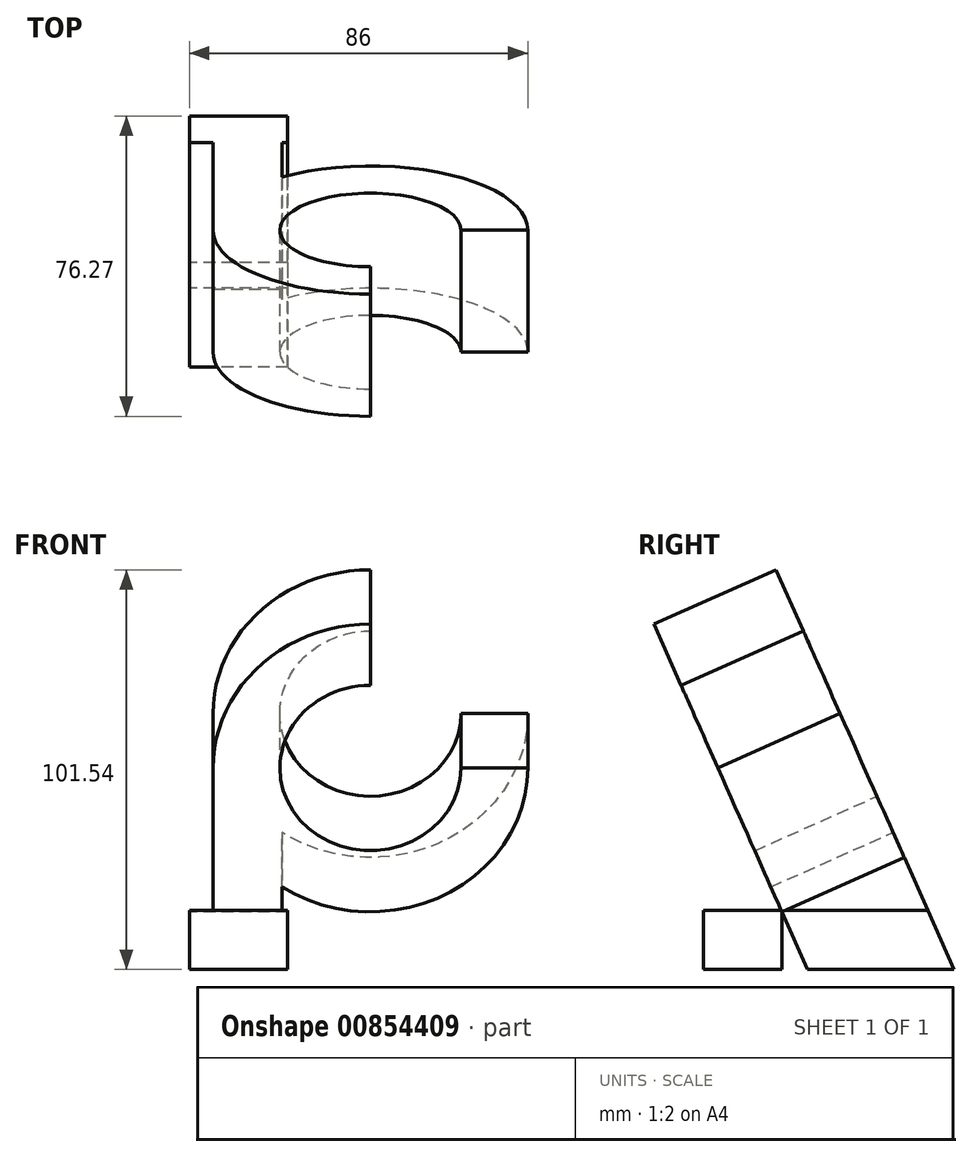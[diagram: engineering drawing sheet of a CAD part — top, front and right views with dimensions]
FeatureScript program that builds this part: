
annotation { "Feature Type Name" : "Feature", "Feature Type Description" : "" }
export const myFeature = defineFeature(function(context is Context, id is Id, definition is map)
    precondition{}
    {
        {
            var Q0;
            Q0=qCreatedBy(makeId("Top.planeOp"),FACE);
            var sketch = newSketch(context, id + "F0", { "sketchPlane" : qUnion([Q0])});
            skLineSegment(sketch, "E0", {"start": v(-57.2, 0) * mm, "end": v(54.58, 0) * mm});
            skSolve(sketch);
        }
        {
            var Q0;
            Q0 = qBodyType(qCreatedBy(id + "F0" ,EDGE), BodyType.WIRE);
            cPlane(context, id + "F1", {"entities" : qUnion([Q0]), "cplaneType" : CPlaneType.LINE_ANGLE, "offset" : 25 * mm, "angle" : 24 * degree, "width" : 150 * mm, "height" : 150 * mm});
        }
        {
            var Q0;
            Q0=qCreatedBy(id+"F1.planeOp",FACE);
            var sketch = newSketch(context, id + "F2", { "sketchPlane" : qUnion([Q0])});
            skCircle(sketch, "E1", {"center": v(0, 0) * mm, "radius": 23 * mm});
            skCircle(sketch, "E2", {"center": v(0, 0) * mm, "radius": 40 * mm});
            skSolve(sketch);
        }
        {
            var Q0;
            Q0=qCreatedBy(makeId("Right.planeOp"),FACE);
            var sketch = newSketch(context, id + "F3", { "sketchPlane" : qUnion([Q0])});
            skPoint(sketch, "E3.0", {"position": v(0, 0) * mm});
            skLineSegment(sketch, "E4.0.0", {"start": v(-9.35, 21.01) * mm, "end": v(9.35, -21.01) * mm});
            skLineSegment(sketch, "E5.0", {"start": v(-16.27, 36.54) * mm, "end": v(16.27, -36.54) * mm});
            skLineSegment(sketch, "E6", {"start": v(-39.16, -65) * mm, "end": v(50.6, -65) * mm});
            skSolve(sketch);
        }
        {
            var Q0;
            Q0=makeQuery(id+"F2.imprint","IMPRINT",FACE,{"disambiguationData":[TD([[makeQuery(id+"F2.imprint","IMPRINT",EDGE,{"derivedFrom":sQuery(id+"F2.wireOp",EDGE,"E1")}),-1.0]])]});
            extrude(context, id + "F4", {"entities" : qUnion([Q0]), "oppositeDirection" : true, "depth" : 34 * mm, "offsetDistance" : 25 * mm});
        }
        {
            var Q0;
            Q0=qCreatedBy(makeId("Right.planeOp"),FACE);
            var sketch = newSketch(context, id + "F5", { "sketchPlane" : qUnion([Q0])});
            skLineSegment(sketch, "E7.0", {"start": v(-47.33, 22.71) * mm, "end": v(-14.8, -50.37) * mm});
            skLineSegment(sketch, "E8", {"start": v(-14.8, -50.37) * mm, "end": v(1.65, -87.3) * mm});
            skLineSegment(sketch, "E9.0", {"start": v(-16.27, 36.54) * mm, "end": v(16.27, -36.54) * mm});
            skLineSegment(sketch, "E10", {"start": v(16.27, -36.54) * mm, "end": v(32.23, -72.39) * mm});
            skLineSegment(sketch, "E11.0", {"start": v(-39.16, -50) * mm, "end": v(50.6, -50) * mm});
            skLineSegment(sketch, "E12", {"start": v(-14.8, -50.37) * mm, "end": v(-14.8, -68.96) * mm});
            skLineSegment(sketch, "E13.0", {"start": v(-39.16, -65) * mm, "end": v(50.6, -65) * mm});
            skLineSegment(sketch, "E14", {"start": v(-14.8, -65) * mm, "end": v(-34.8, -65) * mm});
            skPoint(sketch, "E14.startSnap0", {"position": v(-14.8, -59.67) * mm});
            skLineSegment(sketch, "E15", {"start": v(-14.8, -65) * mm, "end": v(45.2, -65) * mm});
            skLineSegment(sketch, "E16", {"start": v(-34.8, -65) * mm, "end": v(-34.8, -50) * mm});
            skLineSegment(sketch, "E17", {"start": v(45.2, -65) * mm, "end": v(45.2, -50) * mm});
            skSolve(sketch);
        }
        {
            var Q0;
            Q0=qCreatedBy(makeId("Right.planeOp"),FACE);
            cPlane(context, id + "F6", {"entities" : qUnion([Q0]), "cplaneType" : CPlaneType.OFFSET, "offset" : 46 * mm, "oppositeDirection" : true, "width" : 150 * mm, "height" : 150 * mm});
        }
        {
            var Q0;
            Q0=qCreatedBy(id+"F6.planeOp",FACE);
            var sketch = newSketch(context, id + "F7", { "sketchPlane" : qUnion([Q0])});
            skLineSegment(sketch, "E18.0.0", {"start": v(-34.8, -50) * mm, "end": v(-34.8, -65) * mm});
            skLineSegment(sketch, "E18.0.1", {"start": v(-34.8, -65) * mm, "end": v(-14.8, -65) * mm});
            skLineSegment(sketch, "E18.0.2", {"start": v(-14.8, -65) * mm, "end": v(-14.8, -50.37) * mm});
            skLineSegment(sketch, "E18.0.3", {"start": v(-14.8, -50.37) * mm, "end": v(-14.96, -50) * mm});
            skLineSegment(sketch, "E18.0.4", {"start": v(-14.96, -50) * mm, "end": v(-34.8, -50) * mm});
            skLineSegment(sketch, "E19.0.0", {"start": v(-8.28, -65) * mm, "end": v(-14.8, -50.37) * mm});
            skLineSegment(sketch, "E19.0.1", {"start": v(-14.8, -50.37) * mm, "end": v(-14.8, -65) * mm});
            skLineSegment(sketch, "E19.0.2", {"start": v(-14.8, -65) * mm, "end": v(-8.28, -65) * mm});
            skLineSegment(sketch, "E20.0.0", {"start": v(22.26, -50) * mm, "end": v(-14.96, -50) * mm});
            skLineSegment(sketch, "E20.0.1", {"start": v(-14.96, -50) * mm, "end": v(-14.8, -50.37) * mm});
            skLineSegment(sketch, "E20.0.2", {"start": v(-14.8, -50.37) * mm, "end": v(-8.28, -65) * mm});
            skLineSegment(sketch, "E20.0.3", {"start": v(-8.28, -65) * mm, "end": v(28.94, -65) * mm});
            skLineSegment(sketch, "E20.0.4", {"start": v(28.94, -65) * mm, "end": v(22.26, -50) * mm});
            skLineSegment(sketch, "E21.0.0", {"start": v(22.26, -50) * mm, "end": v(28.94, -65) * mm});
            skLineSegment(sketch, "E21.0.1", {"start": v(28.94, -65) * mm, "end": v(45.2, -65) * mm});
            skLineSegment(sketch, "E21.0.2", {"start": v(45.2, -65) * mm, "end": v(45.2, -50) * mm});
            skLineSegment(sketch, "E21.0.3", {"start": v(45.2, -50) * mm, "end": v(22.26, -50) * mm});
            skSolve(sketch);
        }
        {
            var Q0;
            Q0=makeQuery(id+"F7.imprint","IMPRINT",FACE,{"disambiguationData":[TD([[makeQuery(id+"F7.imprint","IMPRINT",EDGE,{"derivedFrom":sQuery(id+"F7.wireOp",EDGE,"E21.0.0")}),1.0]])]});
            var Q1;
            Q1=makeQuery(id+"F7.imprint","IMPRINT",FACE,{"disambiguationData":[TD([[makeQuery(id+"F7.imprint","IMPRINT",EDGE,{"derivedFrom":sQuery(id+"F7.wireOp",EDGE,"E20.0.0")}),1.0]])]});
            var Q2;
            Q2=makeQuery(id+"F7.imprint","IMPRINT",FACE,{"disambiguationData":[TD([[makeQuery(id+"F7.imprint","IMPRINT",EDGE,{"derivedFrom":sQuery(id+"F7.wireOp",EDGE,"E19.0.1")}),1.0]])]});
            var Q3;
            Q3=makeQuery(id+"F7.imprint","IMPRINT",FACE,{"disambiguationData":[TD([[makeQuery(id+"F7.imprint","IMPRINT",EDGE,{"derivedFrom":sQuery(id+"F7.wireOp",EDGE,"E18.0.0")}),1.0]])]});
            extrude(context, id + "F8", {"entities" : qUnion([Q0, Q1, Q2, Q3]), "depth" : 25 * mm, "offsetDistance" : 25 * mm});
        }
        {
            var Q0;
            Q0=qCreatedBy(id+"F1.planeOp",FACE);
            var sketch = newSketch(context, id + "F9", { "sketchPlane" : qUnion([Q0])});
            skCircle(sketch, "E22.0.0", {"center": v(0, 0) * mm, "radius": 40 * mm});
            skLineSegment(sketch, "E23.0", {"start": v(57.2, 0) * mm, "end": v(-54.58, 0) * mm});
            skLineSegment(sketch, "E24", {"start": v(40, 0) * mm, "end": v(40, -135.38) * mm});
            skLineSegment(sketch, "E25", {"start": v(22.5, 0) * mm, "end": v(22.5, -138.62) * mm});
            skLineSegment(sketch, "E26", {"start": v(22.5, -125.31) * mm, "end": v(40, -125.31) * mm});
            skSolve(sketch);
        }
        {
            var Q0;
            {var subQ5=sQuery(id+"F9.wireOp",EDGE,"E26");Q0=makeQuery(id+"F9.imprint","IMPRINT",FACE,{"disambiguationData":[TD([[makeQuery(id+"F9.imprint","IMPRINT",EDGE,{"derivedFrom":subQ5}),1.0]])]});}
            var Q1;
            Q1=makeQuery(id+"F4.opExtrude","CAP_FACE",FACE,{"disambiguationData":[OSD([sQuery(id+"F2.wireOp",EDGE,"E1"),sQuery(id+"F2.wireOp",EDGE,"E2")])],"isStart":false});
            extrude(context, id + "F10", {"entities" : qUnion([Q0]), "operationType" : NewBodyOperationType.ADD, "endBound" : BoundingType.UP_TO_SURFACE, "oppositeDirection" : true, "depth" : 25 * mm, "endBoundEntityFace" : qUnion([Q1]), "offsetDistance" : 25 * mm});
        }
        {
            var Q0;
            {var subQ0=sQuery(id+"F9.wireOp",EDGE,"E26");var subQ1=sQuery(id+"F9.wireOp",EDGE,"E25");Q0=makeQuery(id+"F10.boolean.opBoolean","SPLIT",FACE,{"disambiguationData":[TD([makeQuery(id+"F10.opExtrude","SWEPT_FACE",FACE,{"disambiguationData":[OSD([subQ0])]})])],"derivedFrom":makeQuery(id+"F10.opExtrude","SWEPT_FACE",FACE,{"disambiguationData":[OSD([subQ1])]})});}
            extrude(context, id + "F11", {"entities" : qUnion([Q0]), "operationType" : NewBodyOperationType.REMOVE, "oppositeDirection" : true, "depth" : 133 * mm, "offsetDistance" : 25 * mm});
        }
        {
            var Q0;
            Q0=makeQuery(id+"F10.boolean.opBoolean","MERGE",FACE,{"derivedFrom":[makeQuery(id+"F4.opExtrude","CAP_FACE",FACE,{"disambiguationData":[OSD([sQuery(id+"F2.wireOp",EDGE,"E1"),sQuery(id+"F2.wireOp",EDGE,"E2")])],"isStart":true}),makeQuery(id+"F10.opExtrude","CAP_FACE",FACE,{"disambiguationData":[OSD([sQuery(id+"F9.wireOp",EDGE,"E22.0.0"),sQuery(id+"F9.wireOp",EDGE,"E24"),sQuery(id+"F9.wireOp",EDGE,"E25"),sQuery(id+"F9.wireOp",EDGE,"E26")])],"isStart":true})]});
            var sketch = newSketch(context, id + "F12", { "sketchPlane" : qUnion([Q0])});
            skArc(sketch, "E27.0.0", {"start": v(40, 0) * mm, "mid": v(-35.36, 18.7) * mm, "end": v(22.5, -33.07) * mm});
            skLineSegment(sketch, "E27.0.1", {"start": v(22.5, -33.07) * mm, "end": v(22.5, -54.73) * mm});
            skLineSegment(sketch, "E27.0.2", {"start": v(22.5, -54.73) * mm, "end": v(40, -54.73) * mm});
            skLineSegment(sketch, "E27.0.3", {"start": v(40, -54.73) * mm, "end": v(40, 0) * mm});
            skCircle(sketch, "E28.0", {"center": v(0, 0) * mm, "radius": 23 * mm});
            skLineSegment(sketch, "E29", {"start": v(0, 23) * mm, "end": v(0, 40) * mm});
            skLineSegment(sketch, "E30", {"start": v(-23, 0) * mm, "end": v(-40, 0) * mm});
            skSolve(sketch);
        }
        {
            var Q0;
            {var subQ0=sQuery(id+"F12.wireOp",EDGE,"E29");Q0=makeQuery(id+"F12.imprint","IMPRINT",FACE,{"disambiguationData":[TD([[makeQuery(id+"F12.imprint","IMPRINT",EDGE,{"derivedFrom":subQ0}),1.0]])]});}
            extrude(context, id + "F13", {"entities" : qUnion([Q0]), "operationType" : NewBodyOperationType.REMOVE, "oppositeDirection" : true, "depth" : 262 * mm, "offsetDistance" : 25 * mm});
        }
    });
